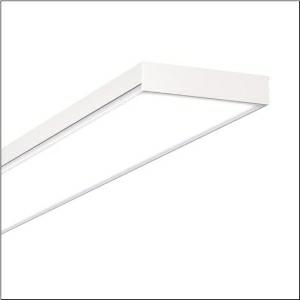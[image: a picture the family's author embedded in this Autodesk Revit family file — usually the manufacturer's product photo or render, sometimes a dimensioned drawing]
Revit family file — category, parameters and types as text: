
# Revit family: apollon_r__31_surface_51mp26wm2441wa_f345
name_source: partatom
category: Lighting Fixtures
units: mm (PartAtom-declared; Revit-internal decimal feet)

## family parameters
Cut with Voids When Loaded = No
Host = Face
Light Source = No
Part Type = Normal
Room Calculation Point = No
Round Connector Dimension = Use Diameter
Shared = No

## types (1)
- Apollon® 31 Surface (1 x LED, 4600 lm, 33 W, 4000K)
    Apparent Load = 33 VA
    CIE Flux Codes = 61 87 97 97 100
    Color Rendering = 80
    Color Temperature = 4000K
    Default Elevation = 1800 mm
    Description = Apollon® 31 Surface, office luminaire, primary optical cover: micro prismatic cover, of PMMA, light emission: direct distribution, primary light characteristic: symmetric, installation type: surface-mounted, LED, rated luminous flux: 4.600lm, luminous efficacy: 139lm/W, light colour: 840, colour temperature: 4000K, control gear: ON/OFF Multilumen, with terminal, 3-pole, mains connection: 220..240V, AC, 50/60Hz, rated input power: 33W, housing, of sheet steel, coil coated, traffic white (RAL 9016), length: 1.545mm, width: 200mm, height: 44mm, protection rating (complete): IP20, insulation class (complete): insulation class II (safety insulation), certification: CE, impact resistance: IK02, permissible operating ambient temperature: -20..+40°C, packaging unit: 1 piece
    Height = 44 mm
    Lamp = 1 x LED
    Lamp Light Flux = 4600 lm
    Lamp Power = 33 W
    Lamp count = 1
    Length = 1545 mm
    Luminous efficacy = 139 lm/W
    Manufacturer = Siteco
    ModVariant = No
    Model = 51MP26WM2441WA
    Mounting Place = Ceiling
    Mounting Type = Surface mounted
    Number of Poles = 1
    OnlyDefault = Yes
    Power Factor = 1
    Product Name = Apollon® 31 Surface
    Product group = office luminaire | ceiling mounted
    ProductGroupID = 302
    Protection Class = Protection class II
    Protection Degree = IP 20
    RLX_Detail_Level = 1
    RLX_Emergency_Light_Flux = 0 lm
    RLX_Emergency_Type = 0
    RLX_Emergency_Type_DB = No
    RlxData = <blob elided: 20757 chars, md5=c7930ae3>
    Socket = socket
    Standby Power = 0 W
    System Light Flux = 4600 lm
    System Power = 33 W
    Type Comments = Product without accessories
    Type Image = l_1313658.jpg
    URL = http://relux.com
    VarID = ---
    Voltage = 0 V
    Weight = 0.00 kg
    Width = 200 mm  [stored 0.656168 ft]

note: [stored X ft] marks values corroborated as IEEE doubles in the binary element streams (Revit-internal decimal feet)

## geometry (parser evidence)
native form markers: Blend x4, Sweep x11
no freeform markers — native parametric forms only
